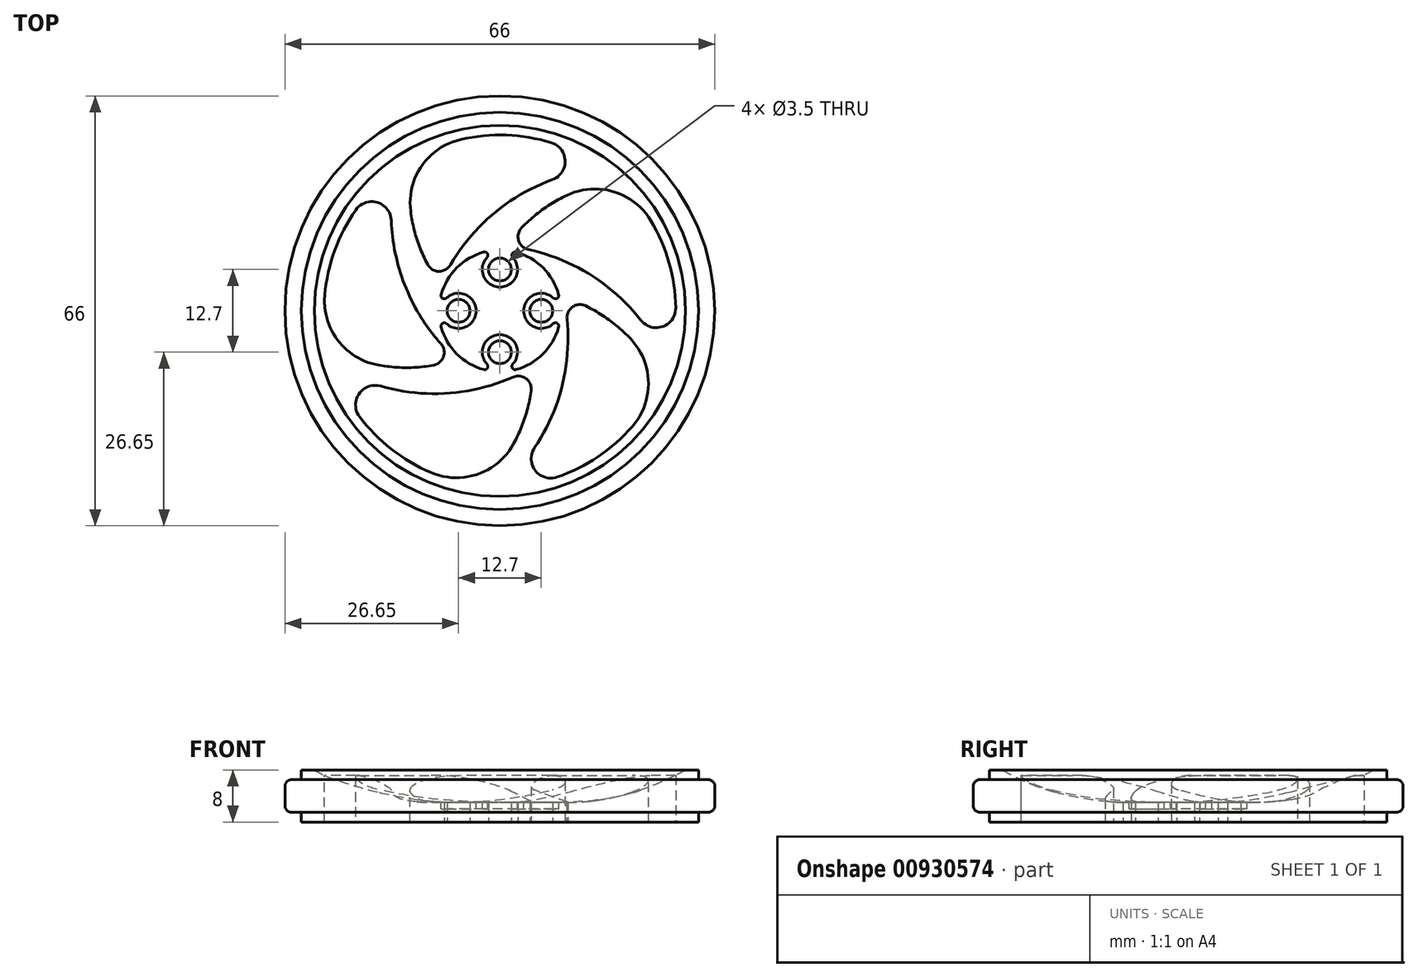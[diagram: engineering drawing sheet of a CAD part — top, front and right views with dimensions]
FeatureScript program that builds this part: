
annotation { "Feature Type Name" : "Feature", "Feature Type Description" : "" }
export const myFeature = defineFeature(function(context is Context, id is Id, definition is map)
    precondition{}
    {
        {
            var Q0;
            Q0=qCreatedBy(makeId("Front.planeOp"),FACE);
            var sketch = newSketch(context, id + "F0", { "sketchPlane" : qUnion([Q0])});
            skLineSegment(sketch, "E0.right", {"start": v(33, 1.5) * mm, "end": v(33, 6.5) * mm});
            skLineSegment(sketch, "E1", {"start": v(30.5, 6.5) * mm, "end": v(33, 6.5) * mm});
            skLineSegment(sketch, "E2", {"start": v(30.5, 6.5) * mm, "end": v(30.5, 8) * mm});
            skLineSegment(sketch, "E3.MirrorCS", {"start": v(30.5, 1.5) * mm, "end": v(30.5, 0) * mm});
            skLineSegment(sketch, "E4.MirrorCS", {"start": v(30.5, 1.5) * mm, "end": v(33, 1.5) * mm});
            skLineSegment(sketch, "E5.trimOffspring", {"start": v(28.5, 8) * mm, "end": v(30.5, 8) * mm});
            skLineSegment(sketch, "E6", {"start": v(0, 0) * mm, "end": v(30.5, 0) * mm});
            skLineSegment(sketch, "E7", {"start": v(0, 0) * mm, "end": v(0, 3) * mm});
            skLineSegment(sketch, "E8", {"start": v(0, 3) * mm, "end": v(10, 3) * mm});
            skArc(sketch, "E9", {"start": v(10, 3) * mm, "mid": v(19.58, 4.27) * mm, "end": v(28.5, 8) * mm});
            skSolve(sketch);
        }
        {
            var Q0;
            Q0=qSketchRegion(id+"F0",true);
            var Q1;
            Q1=sQuery(id+"F0.wireOp",EDGE,"E7");
            revolve(context, id + "F1", {"entities" : qUnion([Q0]), "axis" : qUnion([Q1]), "revolveType" : RevolveType.FULL});
        }
        {
            var Q0;
            Q0=makeQuery(id+"F1.opRevolve","SWEPT_EDGE",EDGE,{"disambiguationData":[OSD([sQuery(id+"F0.wireOp",EDGE,"E0.right"),sQuery(id+"F0.wireOp",EDGE,"E1")])]});
            var Q1;
            Q1=makeQuery(id+"F1.opRevolve","SWEPT_EDGE",EDGE,{"disambiguationData":[OSD([sQuery(id+"F0.wireOp",EDGE,"E0.right"),sQuery(id+"F0.wireOp",EDGE,"E4.MirrorCS")])]});
            fillet(context, id + "F2", {"entities" : qUnion([Q0, Q1]), "radius" : 1 * mm, "tangentPropagation" : true, "allowEdgeOverflow" : false});
        }
        {
            var Q0;
            Q0=makeQuery(id+"F1.opRevolve","SWEPT_FACE",FACE,{"disambiguationData":[OSD([sQuery(id+"F0.wireOp",EDGE,"E6")])]});
            var sketch = newSketch(context, id + "F3", { "sketchPlane" : qUnion([Q0])});
            skCircle(sketch, "E10", {"center": v(0, 0) * mm, "radius": 10 * mm, "construction": true});
            skCircle(sketch, "E11", {"center": v(0, 0) * mm, "radius": 28.5 * mm, "construction": true});
            skArc(sketch, "E12", {"start": v(-3, 26.83) * mm, "mid": v(-17.06, 20.93) * mm, "end": v(-25.68, 8.34) * mm});
            skArc(sketch, "E13.trimOffspring", {"start": v(-26.45, 5.44) * mm, "mid": v(-25.18, -9.76) * mm, "end": v(-15.87, -21.84) * mm});
            skArc(sketch, "E14.trimOffspring", {"start": v(18.2, -19.95) * mm, "mid": v(26.1, -6.9) * mm, "end": v(25.68, 8.34) * mm});
            skLineSegment(sketch, "E15", {"start": v(0, 28.5) * mm, "end": v(0, 0) * mm, "construction": true});
            skLineSegment(sketch, "E16", {"start": v(0, 0) * mm, "end": v(-25.68, 8.34) * mm, "construction": true});
            skLineSegment(sketch, "E17", {"start": v(0, 0) * mm, "end": v(25.68, 8.34) * mm, "construction": true});
            skLineSegment(sketch, "E18", {"start": v(0, 0) * mm, "end": v(-15.87, -21.84) * mm, "construction": true});
            skLineSegment(sketch, "E19", {"start": v(0, 0) * mm, "end": v(15.87, -21.84) * mm, "construction": true});
            skArc(sketch, "E20.trimOffspring", {"start": v(24.6, 11.14) * mm, "mid": v(14.63, 22.7) * mm, "end": v(0, 27) * mm});
            skArc(sketch, "E21.trimOffspring", {"start": v(-13.35, -23.47) * mm, "mid": v(1.5, -26.96) * mm, "end": v(15.87, -21.84) * mm});
            skArc(sketch, "E22", {"start": v(9.77, -2.12) * mm, "mid": v(8.9, 13.79) * mm, "end": v(0, 27) * mm});
            skArc(sketch, "E23", {"start": v(1, -9.95) * mm, "mid": v(15.86, -4.2) * mm, "end": v(25.68, 8.34) * mm});
            skArc(sketch, "E24", {"start": v(-9.15, -4.03) * mm, "mid": v(0.9, -16.38) * mm, "end": v(15.87, -21.84) * mm});
            skArc(sketch, "E25", {"start": v(-6.66, 7.46) * mm, "mid": v(-15.3, -5.92) * mm, "end": v(-15.87, -21.84) * mm});
            skArc(sketch, "E26", {"start": v(5.04, 8.64) * mm, "mid": v(-10.36, 12.72) * mm, "end": v(-25.68, 8.34) * mm});
            skArc(sketch, "E27", {"start": v(-6.66, 7.46) * mm, "mid": v(-16.77, 8.6) * mm, "end": v(-26.45, 5.44) * mm});
            skArc(sketch, "E28", {"start": v(5.04, 8.64) * mm, "mid": v(3, 18.6) * mm, "end": v(-3, 26.83) * mm});
            skArc(sketch, "E29", {"start": v(9.77, -2.12) * mm, "mid": v(18.62, 2.9) * mm, "end": v(24.6, 11.14) * mm});
            skArc(sketch, "E30", {"start": v(1, -9.95) * mm, "mid": v(8.52, -16.81) * mm, "end": v(18.2, -19.95) * mm});
            skArc(sketch, "E31", {"start": v(-9.15, -4.03) * mm, "mid": v(-13.36, -13.3) * mm, "end": v(-13.35, -23.47) * mm});
            skCircle(sketch, "E32", {"center": v(0, -6.35) * mm, "radius": 1.75 * mm});
            skCircle(sketch, "E33", {"center": v(-6.35, 0) * mm, "radius": 1.75 * mm});
            skCircle(sketch, "E34", {"center": v(6.35, 0) * mm, "radius": 1.75 * mm});
            skCircle(sketch, "E35", {"center": v(0, 6.35) * mm, "radius": 1.75 * mm});
            skSolve(sketch);
        }
        {
            var Q0;
            Q0=qSketchRegion(id+"F3",true);
            extrude(context, id + "F4", {"entities" : qUnion([Q0]), "operationType" : NewBodyOperationType.REMOVE, "oppositeDirection" : true, "depth" : 25 * mm});
        }
        {
            var Q0;
            Q0=makeQuery(id+"F4.boolean.opBoolean","COPY",EDGE,{"derivedFrom":makeQuery(id+"F4.opExtrude","SWEPT_EDGE",EDGE,{"disambiguationData":[OSD([sQuery(id+"F3.wireOp",EDGE,"E20.trimOffspring"),sQuery(id+"F3.wireOp",EDGE,"E22")])]})});
            var Q1;
            Q1=makeQuery(id+"F4.boolean.opBoolean","COPY",EDGE,{"derivedFrom":makeQuery(id+"F4.opExtrude","SWEPT_EDGE",EDGE,{"disambiguationData":[OSD([sQuery(id+"F3.wireOp",EDGE,"E12"),sQuery(id+"F3.wireOp",EDGE,"E26")])]})});
            var Q2;
            Q2=makeQuery(id+"F4.boolean.opBoolean","COPY",EDGE,{"derivedFrom":makeQuery(id+"F4.opExtrude","SWEPT_EDGE",EDGE,{"disambiguationData":[OSD([sQuery(id+"F3.wireOp",EDGE,"E13.trimOffspring"),sQuery(id+"F3.wireOp",EDGE,"E25")])]})});
            var Q3;
            Q3=makeQuery(id+"F4.boolean.opBoolean","COPY",EDGE,{"derivedFrom":makeQuery(id+"F4.opExtrude","SWEPT_EDGE",EDGE,{"disambiguationData":[OSD([sQuery(id+"F3.wireOp",EDGE,"E21.trimOffspring"),sQuery(id+"F3.wireOp",EDGE,"E24")])]})});
            var Q4;
            Q4=makeQuery(id+"F4.boolean.opBoolean","COPY",EDGE,{"derivedFrom":makeQuery(id+"F4.opExtrude","SWEPT_EDGE",EDGE,{"disambiguationData":[OSD([sQuery(id+"F3.wireOp",EDGE,"E14.trimOffspring"),sQuery(id+"F3.wireOp",EDGE,"E23")])]})});
            fillet(context, id + "F5", {"entities" : qUnion([Q0, Q1, Q2, Q3, Q4]), "radius" : 3 * mm, "tangentPropagation" : true, "allowEdgeOverflow" : false});
        }
        {
            var Q0;
            Q0=makeQuery(id+"F4.boolean.opBoolean","COPY",EDGE,{"derivedFrom":makeQuery(id+"F4.opExtrude","SWEPT_EDGE",EDGE,{"disambiguationData":[OSD([sQuery(id+"F3.wireOp",EDGE,"E14.trimOffspring"),sQuery(id+"F3.wireOp",EDGE,"E30")])]})});
            var Q1;
            Q1=makeQuery(id+"F4.boolean.opBoolean","COPY",EDGE,{"derivedFrom":makeQuery(id+"F4.opExtrude","SWEPT_EDGE",EDGE,{"disambiguationData":[OSD([sQuery(id+"F3.wireOp",EDGE,"E20.trimOffspring"),sQuery(id+"F3.wireOp",EDGE,"E29")])]})});
            var Q2;
            Q2=makeQuery(id+"F4.boolean.opBoolean","COPY",EDGE,{"derivedFrom":makeQuery(id+"F4.opExtrude","SWEPT_EDGE",EDGE,{"disambiguationData":[OSD([sQuery(id+"F3.wireOp",EDGE,"E12"),sQuery(id+"F3.wireOp",EDGE,"E28")])]})});
            var Q3;
            Q3=makeQuery(id+"F4.boolean.opBoolean","COPY",EDGE,{"derivedFrom":makeQuery(id+"F4.opExtrude","SWEPT_EDGE",EDGE,{"disambiguationData":[OSD([sQuery(id+"F3.wireOp",EDGE,"E13.trimOffspring"),sQuery(id+"F3.wireOp",EDGE,"E27")])]})});
            var Q4;
            Q4=makeQuery(id+"F4.boolean.opBoolean","COPY",EDGE,{"derivedFrom":makeQuery(id+"F4.opExtrude","SWEPT_EDGE",EDGE,{"disambiguationData":[OSD([sQuery(id+"F3.wireOp",EDGE,"E21.trimOffspring"),sQuery(id+"F3.wireOp",EDGE,"E31")])]})});
            fillet(context, id + "F6", {"entities" : qUnion([Q0, Q1, Q2, Q3, Q4]), "radius" : 10 * mm, "tangentPropagation" : true, "allowEdgeOverflow" : false});
        }
        {
            var Q0;
            Q0=makeQuery(id+"F4.boolean.opBoolean","COPY",EDGE,{"derivedFrom":makeQuery(id+"F4.opExtrude","SWEPT_EDGE",EDGE,{"disambiguationData":[OSD([sQuery(id+"F3.wireOp",EDGE,"E25"),sQuery(id+"F3.wireOp",EDGE,"E27")])]})});
            var Q1;
            Q1=makeQuery(id+"F4.boolean.opBoolean","COPY",EDGE,{"derivedFrom":makeQuery(id+"F4.opExtrude","SWEPT_EDGE",EDGE,{"disambiguationData":[OSD([sQuery(id+"F3.wireOp",EDGE,"E24"),sQuery(id+"F3.wireOp",EDGE,"E31")])]})});
            var Q2;
            Q2=makeQuery(id+"F4.boolean.opBoolean","COPY",EDGE,{"derivedFrom":makeQuery(id+"F4.opExtrude","SWEPT_EDGE",EDGE,{"disambiguationData":[OSD([sQuery(id+"F3.wireOp",EDGE,"E23"),sQuery(id+"F3.wireOp",EDGE,"E30")])]})});
            var Q3;
            Q3=makeQuery(id+"F4.boolean.opBoolean","COPY",EDGE,{"derivedFrom":makeQuery(id+"F4.opExtrude","SWEPT_EDGE",EDGE,{"disambiguationData":[OSD([sQuery(id+"F3.wireOp",EDGE,"E22"),sQuery(id+"F3.wireOp",EDGE,"E29")])]})});
            var Q4;
            Q4=makeQuery(id+"F4.boolean.opBoolean","COPY",EDGE,{"derivedFrom":makeQuery(id+"F4.opExtrude","SWEPT_EDGE",EDGE,{"disambiguationData":[OSD([sQuery(id+"F3.wireOp",EDGE,"E26"),sQuery(id+"F3.wireOp",EDGE,"E28")])]})});
            fillet(context, id + "F7", {"entities" : qUnion([Q0, Q1, Q2, Q3, Q4]), "radius" : 2 * mm, "tangentPropagation" : true, "allowEdgeOverflow" : false});
        }
        {
            var Q0;
            Q0=makeQuery(id+"F1.opRevolve","SWEPT_FACE",FACE,{"disambiguationData":[OSD([sQuery(id+"F0.wireOp",EDGE,"E8")])]});
            var sketch = newSketch(context, id + "F8", { "sketchPlane" : qUnion([Q0])});
            skArc(sketch, "E36", {"start": v(-9.02, -2.47) * mm, "mid": v(-6.61, -6.61) * mm, "end": v(-2.47, -9.02) * mm});
            skArc(sketch, "E37", {"start": v(-1.97, 8.2) * mm, "mid": v(0, 3.65) * mm, "end": v(1.97, 8.2) * mm});
            skArc(sketch, "E38", {"start": v(-8.2, -1.97) * mm, "mid": v(-3.65, 0) * mm, "end": v(-8.2, 1.97) * mm});
            skArc(sketch, "E39", {"start": v(1.97, -8.2) * mm, "mid": v(0, -3.65) * mm, "end": v(-1.97, -8.2) * mm});
            skArc(sketch, "E40", {"start": v(8.2, 1.97) * mm, "mid": v(3.65, 0) * mm, "end": v(8.2, -1.97) * mm});
            skArc(sketch, "E41.trimOffspring", {"start": v(-2.47, 9.02) * mm, "mid": v(-6.61, 6.61) * mm, "end": v(-9.02, 2.47) * mm});
            skArc(sketch, "E42.trimOffspring", {"start": v(9.02, 2.47) * mm, "mid": v(6.61, 6.61) * mm, "end": v(2.47, 9.02) * mm});
            skArc(sketch, "E43.trimOffspring", {"start": v(2.47, -9.02) * mm, "mid": v(6.61, -6.61) * mm, "end": v(9.02, -2.47) * mm});
            skArc(sketch, "E44", {"start": v(-9.02, 2.47) * mm, "mid": v(-8.8, 1.9) * mm, "end": v(-8.2, 1.97) * mm});
            skArc(sketch, "E45", {"start": v(-8.2, -1.97) * mm, "mid": v(-8.8, -1.9) * mm, "end": v(-9.02, -2.47) * mm});
            skArc(sketch, "E46", {"start": v(-2.47, -9.02) * mm, "mid": v(-1.9, -8.8) * mm, "end": v(-1.97, -8.2) * mm});
            skArc(sketch, "E47", {"start": v(1.97, -8.2) * mm, "mid": v(1.9, -8.8) * mm, "end": v(2.47, -9.02) * mm});
            skArc(sketch, "E48", {"start": v(9.02, -2.47) * mm, "mid": v(8.8, -1.9) * mm, "end": v(8.2, -1.97) * mm});
            skArc(sketch, "E49", {"start": v(8.2, 1.97) * mm, "mid": v(8.8, 1.9) * mm, "end": v(9.02, 2.47) * mm});
            skArc(sketch, "E50", {"start": v(2.47, 9.02) * mm, "mid": v(1.9, 8.8) * mm, "end": v(1.97, 8.2) * mm});
            skArc(sketch, "E51", {"start": v(-1.97, 8.2) * mm, "mid": v(-1.9, 8.8) * mm, "end": v(-2.47, 9.02) * mm});
            skSolve(sketch);
        }
        {
            var Q0;
            Q0=qSketchRegion(id+"F8",true);
            extrude(context, id + "F9", {"entities" : qUnion([Q0]), "operationType" : NewBodyOperationType.REMOVE, "oppositeDirection" : true, "depth" : 1 * mm});
        }
    });
